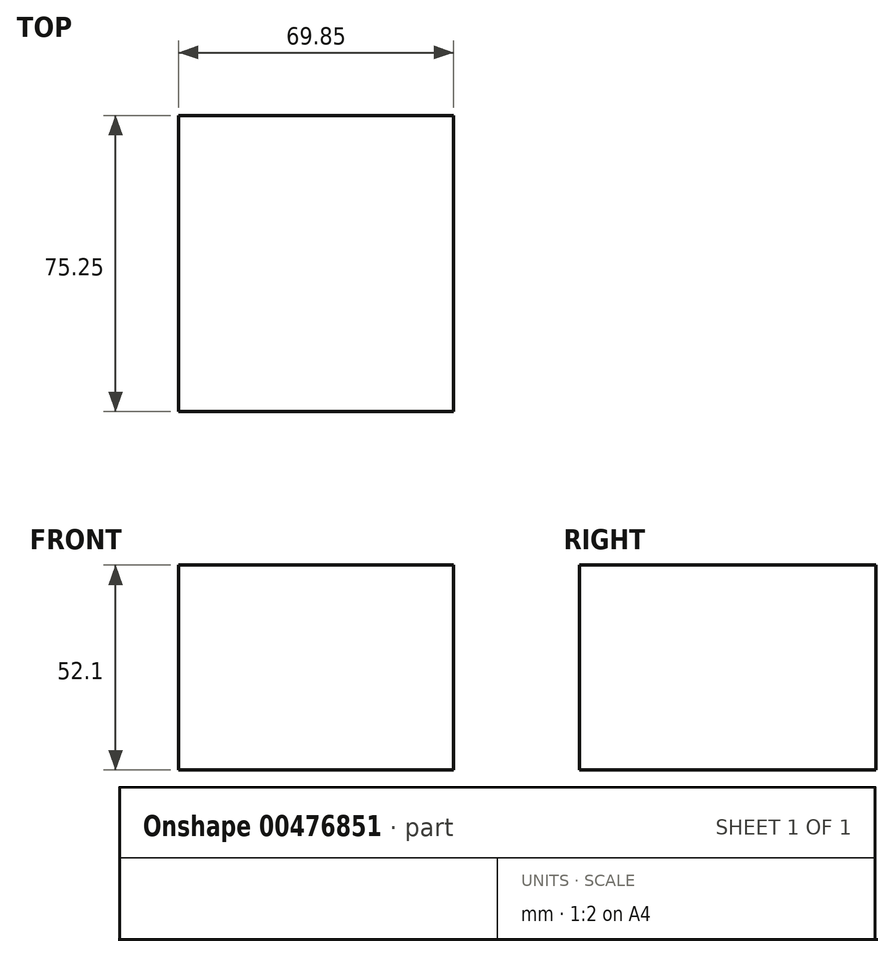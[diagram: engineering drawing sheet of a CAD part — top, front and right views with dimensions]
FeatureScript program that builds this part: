
annotation { "Feature Type Name" : "Feature", "Feature Type Description" : "" }
export const myFeature = defineFeature(function(context is Context, id is Id, definition is map)
    precondition{}
    {
        {
            var Q0;
            Q0=qCreatedBy(makeId("Right.planeOp"),FACE);
            var sketch = newSketch(context, id + "F0", { "sketchPlane" : qUnion([Q0])});
            skLineSegment(sketch, "E0.bottom", {"start": v(-94.96, 106.44) * mm, "end": v(4.78, 106.44) * mm});
            skLineSegment(sketch, "E0.top", {"start": v(-94.96, 33.47) * mm, "end": v(4.78, 33.47) * mm});
            skLineSegment(sketch, "E0.left", {"start": v(-94.96, 106.44) * mm, "end": v(-94.96, 33.47) * mm});
            skLineSegment(sketch, "E0.right", {"start": v(4.78, 106.44) * mm, "end": v(4.78, 33.47) * mm});
            skLineSegment(sketch, "E1.bottom", {"start": v(-94.96, 106.44) * mm, "end": v(-49.57, 106.44) * mm});
            skLineSegment(sketch, "E1.top", {"start": v(-94.96, 74.78) * mm, "end": v(-49.57, 74.78) * mm});
            skLineSegment(sketch, "E1.left", {"start": v(-94.96, 106.44) * mm, "end": v(-94.96, 74.78) * mm});
            skLineSegment(sketch, "E1.right", {"start": v(-49.57, 106.44) * mm, "end": v(-49.57, 74.78) * mm});
            skLineSegment(sketch, "E2.bottom", {"start": v(-94.96, 106.44) * mm, "end": v(-19.7, 106.44) * mm});
            skLineSegment(sketch, "E2.top", {"start": v(-94.96, 54.34) * mm, "end": v(-19.7, 54.34) * mm});
            skLineSegment(sketch, "E2.left", {"start": v(-94.96, 106.44) * mm, "end": v(-94.96, 54.34) * mm});
            skLineSegment(sketch, "E2.right", {"start": v(-19.7, 106.44) * mm, "end": v(-19.7, 54.34) * mm});
            skSolve(sketch);
        }
        {
            var Q0;
            Q0=makeQuery(id+"F0.imprint","IMPRINT",FACE,{"disambiguationData":[TD([[makeQuery(id+"F0.imprint","IMPRINT",EDGE,{"derivedFrom":sQuery(id+"F0.wireOp",EDGE,"E0.bottom")}),-1.0]])]});
            var Q1;
            {var subQ4=sQuery(id+"F0.wireOp",EDGE,"E1.top");Q1=makeQuery(id+"F0.imprint","IMPRINT",FACE,{"disambiguationData":[TD([[makeQuery(id+"F0.imprint","IMPRINT",EDGE,{"derivedFrom":subQ4}),-1.0]])]});}
            var Q2;
            {var subQ0=sQuery(id+"F0.wireOp",EDGE,"E1.top");Q2=makeQuery(id+"F0.imprint","IMPRINT",FACE,{"disambiguationData":[TD([[makeQuery(id+"F0.imprint","IMPRINT",EDGE,{"derivedFrom":subQ0}),1.0]])]});}
            extrude(context, id + "F1", {"entities" : qUnion([Q0, Q1, Q2]), "depth" : 69.85 * mm});
        }
    });
